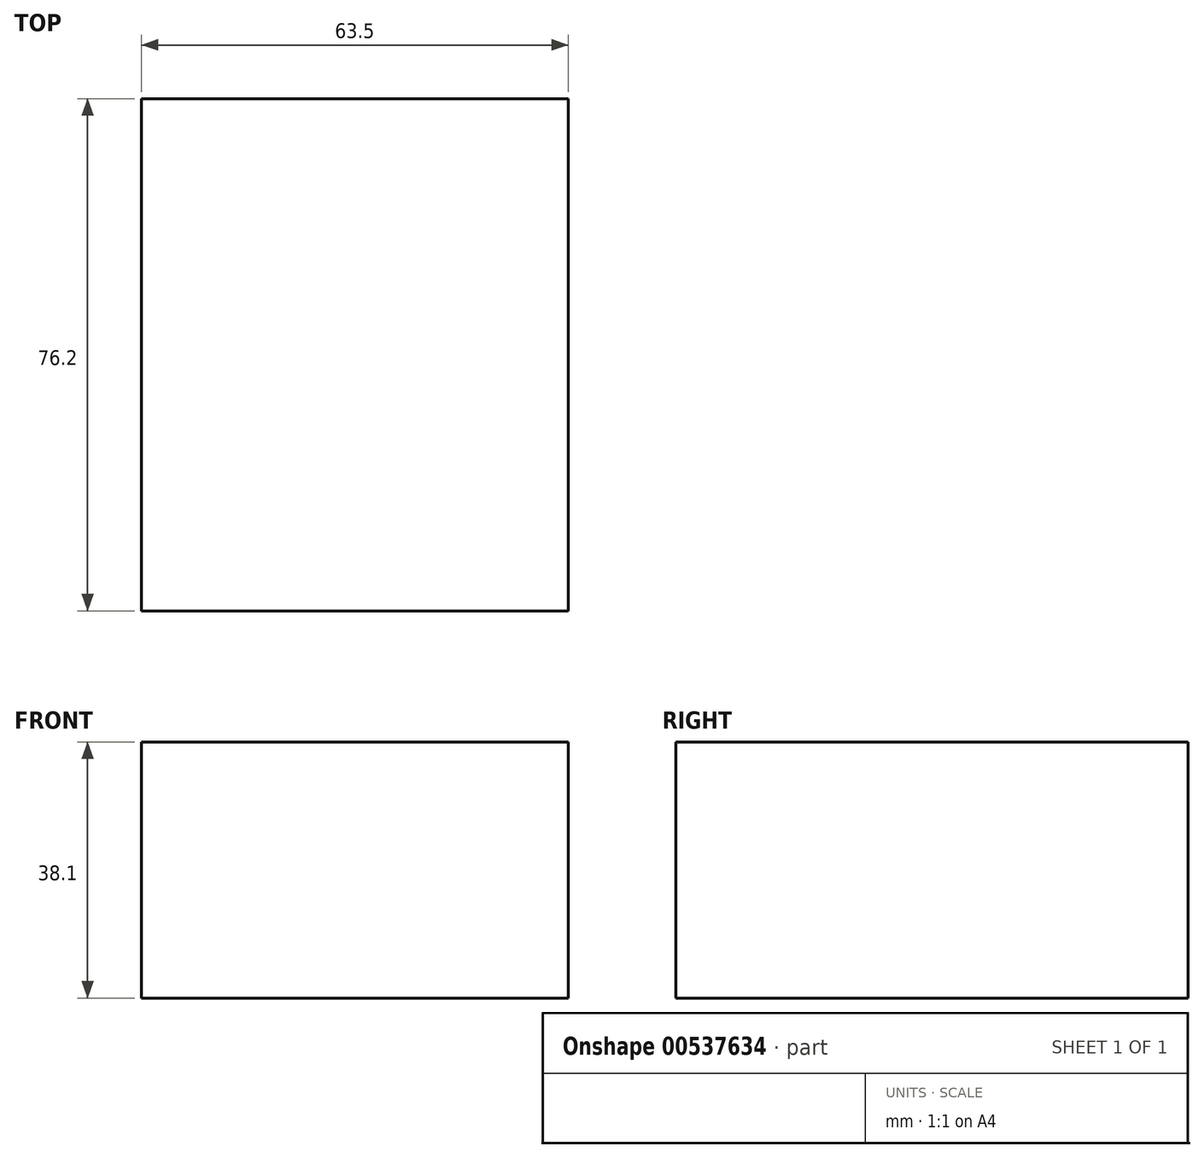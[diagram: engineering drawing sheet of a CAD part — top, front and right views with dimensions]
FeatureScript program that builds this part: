
annotation { "Feature Type Name" : "Feature", "Feature Type Description" : "" }
export const myFeature = defineFeature(function(context is Context, id is Id, definition is map)
    precondition{}
    {
        {
            var Q0;
            Q0=qCreatedBy(makeId("Front.planeOp"),FACE);
            var sketch = newSketch(context, id + "F0", { "sketchPlane" : qUnion([Q0])});
            skLineSegment(sketch, "E0.bottom", {"start": v(-154.32, -85.77) * mm, "end": v(-90.82, -85.77) * mm});
            skLineSegment(sketch, "E0.top", {"start": v(-154.32, -47.67) * mm, "end": v(-90.82, -47.67) * mm});
            skLineSegment(sketch, "E0.left", {"start": v(-154.32, -85.77) * mm, "end": v(-154.32, -47.67) * mm});
            skLineSegment(sketch, "E0.right", {"start": v(-90.82, -85.77) * mm, "end": v(-90.82, -47.67) * mm});
            skSolve(sketch);
        }
        {
            var Q0;
            Q0=makeQuery(id+"F0.imprint","IMPRINT",FACE,{"disambiguationData":[TD([[makeQuery(id+"F0.imprint","IMPRINT",EDGE,{"derivedFrom":sQuery(id+"F0.wireOp",EDGE,"E0.bottom")}),1.0]])]});
            extrude(context, id + "F1", {"entities" : qUnion([Q0]), "depth" : 76.2 * mm, "offsetDistance" : 25.4 * mm});
        }
    });
